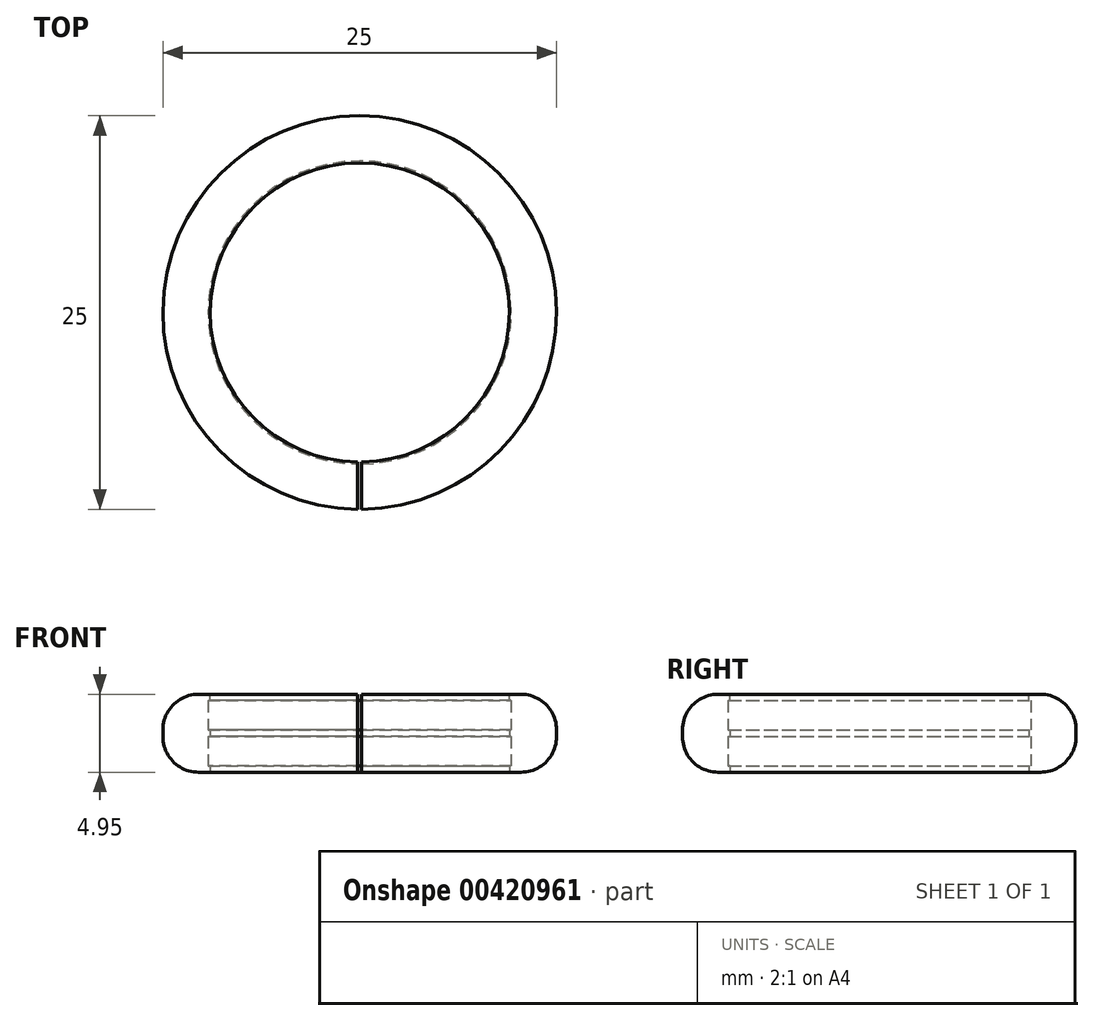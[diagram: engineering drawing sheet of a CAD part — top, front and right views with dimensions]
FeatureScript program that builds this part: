
annotation { "Feature Type Name" : "Feature", "Feature Type Description" : "" }
export const myFeature = defineFeature(function(context is Context, id is Id, definition is map)
    precondition{}
    {
        {
            var Q0;
            Q0=qCreatedBy(makeId("Top.planeOp"),FACE);
            var sketch = newSketch(context, id + "F0", { "sketchPlane" : qUnion([Q0])});
            skCircle(sketch, "E0", {"center": v(0, 0) * mm, "radius": 9.62 * mm});
            skCircle(sketch, "E1", {"center": v(0, 0) * mm, "radius": 12.5 * mm});
            skSolve(sketch);
        }
        {
            var Q0;
            Q0=makeQuery(id+"F0.imprint","IMPRINT",FACE,{"disambiguationData":[TD([[makeQuery(id+"F0.imprint","IMPRINT",EDGE,{"derivedFrom":sQuery(id+"F0.wireOp",EDGE,"E0")}),-1.0]])]});
            extrude(context, id + "F1", {"entities" : qUnion([Q0]), "depth" : 4.95 * mm});
        }
        {
            var Q0;
            Q0=makeQuery(id+"F1.opExtrude","CAP_EDGE",EDGE,{"disambiguationData":[OSD([sQuery(id+"F0.wireOp",EDGE,"E1")])],"isStart":false});
            var Q1;
            Q1=makeQuery(id+"F1.opExtrude","CAP_EDGE",EDGE,{"disambiguationData":[OSD([sQuery(id+"F0.wireOp",EDGE,"E1")])],"isStart":true});
            fillet(context, id + "F2", {"entities" : qUnion([Q0, Q1]), "radius" : 2.25 * mm, "tangentPropagation" : true, "allowEdgeOverflow" : false});
        }
        {
            var Q0;
            Q0=qCreatedBy(makeId("Top.planeOp"),FACE);
            cPlane(context, id + "F3", {"entities" : qUnion([Q0]), "cplaneType" : CPlaneType.OFFSET, "offset" : 2.48 * mm, "width" : 150 * mm, "height" : 150 * mm});
        }
        {
            var Q0;
            Q0=qCreatedBy(id+"F3.planeOp",FACE);
            var sketch = newSketch(context, id + "F4", { "sketchPlane" : qUnion([Q0])});
            skCircle(sketch, "E2", {"center": v(0, 0) * mm, "radius": 9.5 * mm});
            skCircle(sketch, "E3", {"center": v(0, 0) * mm, "radius": 9.62 * mm});
            skSolve(sketch);
        }
        {
            var Q0;
            Q0=makeQuery(id+"F4.imprint","IMPRINT",FACE,{"disambiguationData":[TD([[makeQuery(id+"F4.imprint","IMPRINT",EDGE,{"derivedFrom":sQuery(id+"F4.wireOp",EDGE,"E2")}),-1.0]])]});
            extrude(context, id + "F5", {"entities" : qUnion([Q0]), "operationType" : NewBodyOperationType.ADD, "endBound" : BoundingType.SYMMETRIC, "depth" : 0.4 * mm});
        }
        {
            var Q0;
            Q0=makeQuery(id+"F1.opExtrude","CAP_FACE",FACE,{"disambiguationData":[OSD([sQuery(id+"F0.wireOp",EDGE,"E0"),sQuery(id+"F0.wireOp",EDGE,"E1")])],"isStart":true});
            cPlane(context, id + "F6", {"entities" : qUnion([Q0]), "cplaneType" : CPlaneType.OFFSET, "offset" : 0 * mm, "width" : 150 * mm, "height" : 150 * mm});
        }
        {
            var Q0;
            Q0=qCreatedBy(id+"F6.planeOp",FACE);
            var sketch = newSketch(context, id + "F7", { "sketchPlane" : qUnion([Q0])});
            skCircle(sketch, "E4", {"center": v(0, 0) * mm, "radius": 9.5 * mm});
            skCircle(sketch, "E5", {"center": v(0, 0) * mm, "radius": 9.62 * mm});
            skSolve(sketch);
        }
        {
            var Q0;
            Q0=makeQuery(id+"F7.imprint","IMPRINT",FACE,{"disambiguationData":[TD([[makeQuery(id+"F7.imprint","IMPRINT",EDGE,{"derivedFrom":sQuery(id+"F7.wireOp",EDGE,"E4")}),-1.0]])]});
            extrude(context, id + "F8", {"entities" : qUnion([Q0]), "operationType" : NewBodyOperationType.ADD, "depth" : -.4 * mm});
        }
        {
            var Q0;
            Q0=makeQuery(id+"F1.opExtrude","CAP_FACE",FACE,{"disambiguationData":[OSD([sQuery(id+"F0.wireOp",EDGE,"E0"),sQuery(id+"F0.wireOp",EDGE,"E1")])],"isStart":false});
            cPlane(context, id + "F9", {"entities" : qUnion([Q0]), "cplaneType" : CPlaneType.OFFSET, "offset" : 0 * mm, "width" : 150 * mm, "height" : 150 * mm});
        }
        {
            var Q0;
            Q0=qCreatedBy(id+"F9.planeOp",FACE);
            var sketch = newSketch(context, id + "F10", { "sketchPlane" : qUnion([Q0])});
            skCircle(sketch, "E6", {"center": v(0, 0) * mm, "radius": 9.5 * mm});
            skCircle(sketch, "E7", {"center": v(0, 0) * mm, "radius": 9.62 * mm});
            skLineSegment(sketch, "E8.bottom", {"start": v(0.12, -12.81) * mm, "end": v(-0.13, -12.81) * mm});
            skLineSegment(sketch, "E8.top", {"start": v(0.12, -8.58) * mm, "end": v(-0.13, -8.58) * mm});
            skLineSegment(sketch, "E8.left", {"start": v(0.12, -12.81) * mm, "end": v(0.12, -8.58) * mm});
            skLineSegment(sketch, "E8.right", {"start": v(-0.13, -12.81) * mm, "end": v(-0.13, -8.58) * mm});
            skPoint(sketch, "E8.middle", {"position": v(0, -10.7) * mm});
            skSolve(sketch);
        }
        {
            var Q0;
            Q0=makeQuery(id+"F10.imprint","IMPRINT",FACE,{"disambiguationData":[TD([[makeQuery(id+"F10.imprint","IMPRINT",EDGE,{"derivedFrom":sQuery(id+"F10.wireOp",EDGE,"E6")}),-1.0]])]});
            extrude(context, id + "F11", {"entities" : qUnion([Q0]), "operationType" : NewBodyOperationType.ADD, "depth" : -.4 * mm});
        }
        {
            var Q0;
            {var subQ5=sQuery(id+"F10.wireOp",EDGE,"E8.bottom");Q0=makeQuery(id+"F10.imprint","IMPRINT",FACE,{"disambiguationData":[TD([[makeQuery(id+"F10.imprint","IMPRINT",EDGE,{"derivedFrom":subQ5}),-1.0]])]});}
            var Q1;
            {var subQ0=sQuery(id+"F10.wireOp",EDGE,"E8.left");var subQ1=sQuery(id+"F10.wireOp",EDGE,"E6");var subQ2=makeQuery(id+"F10.imprint","INTERSECT",VERTEX,{"derivedFrom":[subQ1,subQ0]});Q1=makeQuery(id+"F10.imprint","IMPRINT",FACE,{"disambiguationData":[TD([[makeQuery(id+"F10.imprint","IMPRINT",EDGE,{"disambiguationData":[TD([[subQ2,1.0]])],"derivedFrom":subQ1}),-1.0]])]});}
            var Q2;
            {var subQ5=sQuery(id+"F10.wireOp",EDGE,"E8.top");Q2=makeQuery(id+"F10.imprint","IMPRINT",FACE,{"disambiguationData":[TD([[makeQuery(id+"F10.imprint","IMPRINT",EDGE,{"derivedFrom":subQ5}),1.0]])]});}
            extrude(context, id + "F12", {"entities" : qUnion([Q0, Q1, Q2]), "operationType" : NewBodyOperationType.REMOVE, "oppositeDirection" : true, "depth" : 25 * mm});
        }
    });
